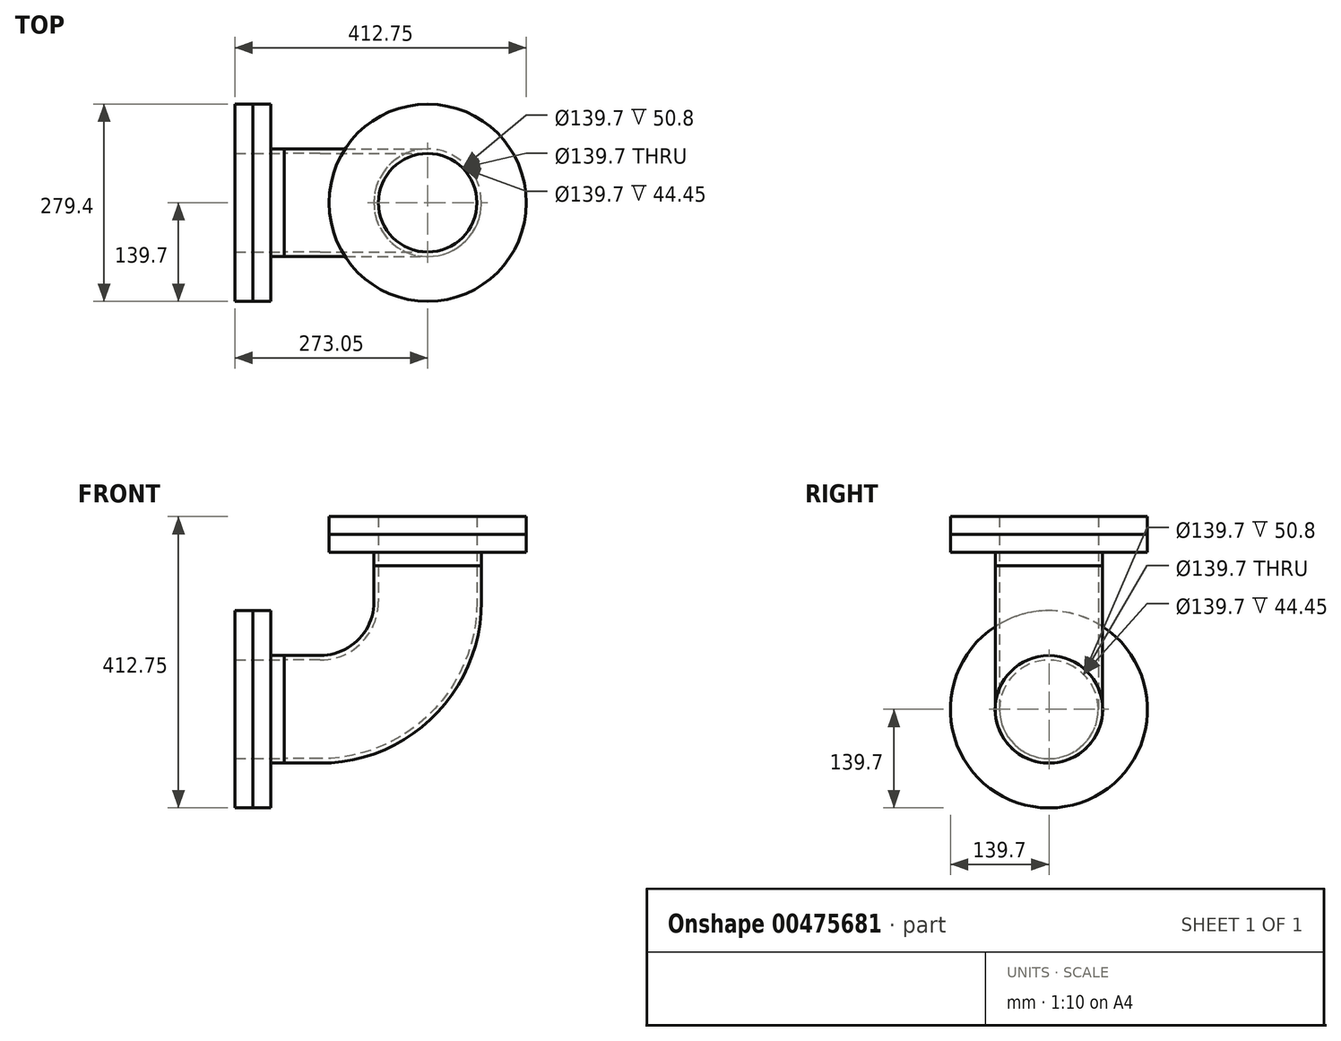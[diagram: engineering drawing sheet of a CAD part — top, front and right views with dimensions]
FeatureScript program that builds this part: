
annotation { "Feature Type Name" : "Feature", "Feature Type Description" : "" }
export const myFeature = defineFeature(function(context is Context, id is Id, definition is map)
    precondition{}
    {
        {
            var Q0;
            Q0=qCreatedBy(makeId("Top.planeOp"),FACE);
            var sketch = newSketch(context, id + "F0", { "sketchPlane" : qUnion([Q0])});
            skCircle(sketch, "E0", {"center": v(0, 0) * mm, "radius": 69.85 * mm});
            skCircle(sketch, "E1", {"center": v(0, 0) * mm, "radius": 76.2 * mm});
            skSolve(sketch);
        }
        {
            var Q0;
            Q0=makeQuery(id+"F0.imprint","IMPRINT",FACE,{"disambiguationData":[TD([[makeQuery(id+"F0.imprint","IMPRINT",EDGE,{"derivedFrom":sQuery(id+"F0.wireOp",EDGE,"E0")}),-1.0]])]});
            extrude(context, id + "F1", {"entities" : qUnion([Q0]), "depth" : 19.05 * mm});
        }
        {
            var Q0;
            Q0=makeQuery(id+"F1.opExtrude","CAP_FACE",FACE,{"disambiguationData":[OSD([sQuery(id+"F0.wireOp",EDGE,"E0"),sQuery(id+"F0.wireOp",EDGE,"E1")])],"isStart":false});
            var sketch = newSketch(context, id + "F2", { "sketchPlane" : qUnion([Q0])});
            skCircle(sketch, "E2", {"center": v(0, 0) * mm, "radius": 139.7 * mm});
            skSolve(sketch);
        }
        {
            var Q0;
            Q0=makeQuery(id+"F2.imprint","IMPRINT",FACE,{"disambiguationData":[TD([[makeQuery(id+"F2.imprint","IMPRINT",EDGE,{"derivedFrom":sQuery(id+"F2.wireOp",EDGE,"E2")}),1.0]])]});
            var Q1;
            Q1=makeQuery(id+"F2.imprint","IMPRINT",FACE,{"disambiguationData":[TD([[makeQuery(id+"F2.imprint","IMPRINT",EDGE,{"derivedFrom":makeQuery(id+"F1.opExtrude","CAP_EDGE",EDGE,{"disambiguationData":[OSD([sQuery(id+"F0.wireOp",EDGE,"E0")])],"isStart":false})}),-1.0]])]});
            extrude(context, id + "F3", {"entities" : qUnion([Q0, Q1]), "operationType" : NewBodyOperationType.ADD, "depth" : 25.4 * mm});
        }
        {
            var Q0;
            Q0=qCreatedBy(makeId("Front.planeOp"),FACE);
            var sketch = newSketch(context, id + "F4", { "sketchPlane" : qUnion([Q0])});
            skLineSegment(sketch, "E3", {"start": v(0, 0) * mm, "end": v(0, -50.8) * mm});
            skLineSegment(sketch, "E4", {"start": v(-152.4, -203.2) * mm, "end": v(-203.2, -203.2) * mm});
            skPoint(sketch, "E5.visualSharp", {"position": v(0, -203.2) * mm});
            skArc(sketch, "E5.filletArc", {"start": v(-152.4, -203.2) * mm, "mid": v(-44.64, -158.56) * mm, "end": v(0, -50.8) * mm});
            skSolve(sketch);
        }
        {
            var Q0;
            Q0=makeQuery(id+"F1.opExtrude","CAP_FACE",FACE,{"disambiguationData":[OSD([sQuery(id+"F0.wireOp",EDGE,"E0"),sQuery(id+"F0.wireOp",EDGE,"E1")])],"isStart":true});
            var Q1;
            Q1=sQuery(id+"F4.wireOp",EDGE,"E5.filletArc");
            var Q2;
            Q2=sQuery(id+"F4.wireOp",EDGE,"E4");
            var Q3;
            Q3=sQuery(id+"F4.wireOp",EDGE,"E3");
            sweep(context, id + "F5", {"profiles" : qUnion([Q0]), "path" : qUnion([Q1, Q2, Q3])});
        }
        {
            var Q0;
            Q0=makeQuery(id+"F5.opSweep","CAP_FACE",FACE,{"disambiguationData":[OSD([sQuery(id+"F0.wireOp",EDGE,"E0"),sQuery(id+"F0.wireOp",EDGE,"E1"),sQuery(id+"F4.wireOp",VERTEX,"E4.end")])],"isStart":false});
            var sketch = newSketch(context, id + "F6", { "sketchPlane" : qUnion([Q0])});
            skPoint(sketch, "E6", {"position": v(0, -203.2) * mm});
            skLineSegment(sketch, "E7", {"start": v(-167.86, -203.2) * mm, "end": v(243.28, -203.2) * mm, "construction": true});
            skSolve(sketch);
        }
        {
            var Q0;
            Q0=makeQuery(id+"F1.opExtrude","SWEPT_BODY",BODY,{"disambiguationData":[OSD([sQuery(id+"F0.wireOp",EDGE,"E0"),sQuery(id+"F0.wireOp",EDGE,"E1")])]});
            var Q1;
            Q1=qCreatedBy(makeId("Origin.pointOp"),VERTEX);
            var Q2;
            Q2=sQuery(id+"F6.wireOp",VERTEX,"E6");
            transform(context, id + "F7", {"entities" : qUnion([Q0]), "transformType" : TransformType.TRANSLATION_ENTITY, "oppositeDirectionEntity" : false, "transformLine" : qUnion([Q1, Q2]), "makeCopy" : true});
        }
        {
            var Q0;
            Q0=makeQuery(id+"F7.opPattern","COPY",BODY,{"derivedFrom":makeQuery(id+"F1.opExtrude","SWEPT_BODY",BODY,{"disambiguationData":[OSD([sQuery(id+"F0.wireOp",EDGE,"E0"),sQuery(id+"F0.wireOp",EDGE,"E1")])]}),"instanceName":"1"});
            var Q1;
            Q1=sQuery(id+"F6.wireOp",EDGE,"E7");
            transform(context, id + "F8", {"entities" : qUnion([Q0]), "transformType" : TransformType.ROTATION, "transformAxis" : qUnion([Q1]), "angle" : 90 * degree, "makeCopy" : false});
        }
        {
            var Q0;
            Q0=makeQuery(id+"F3.opExtrude","CAP_FACE",FACE,{"disambiguationData":[OSD([sQuery(id+"F0.wireOp",EDGE,"E0"),sQuery(id+"F2.wireOp",EDGE,"E2")])],"isStart":false});
            extrude(context, id + "F9", {"entities" : qUnion([Q0]), "depth" : 25.4 * mm});
        }
        {
            var Q0;
            Q0=makeQuery(id+"F7.opPattern","COPY",FACE,{"derivedFrom":makeQuery(id+"F3.opExtrude","CAP_FACE",FACE,{"disambiguationData":[OSD([sQuery(id+"F0.wireOp",EDGE,"E0"),sQuery(id+"F2.wireOp",EDGE,"E2")])],"isStart":false}),"instanceName":"1"});
            extrude(context, id + "F10", {"entities" : qUnion([Q0]), "depth" : 25.4 * mm});
        }
    });
